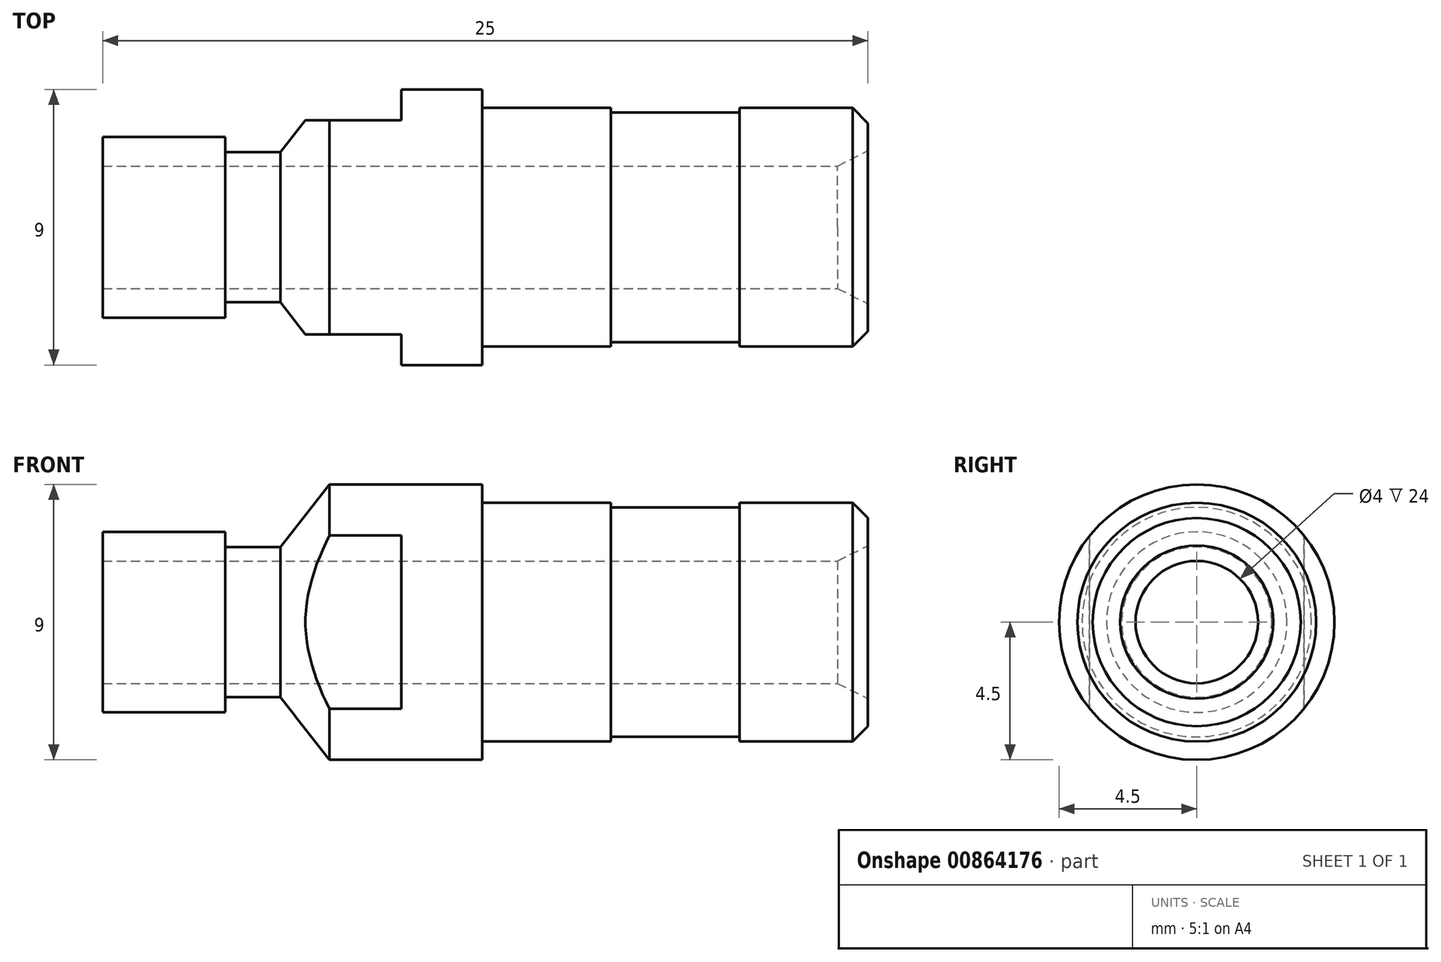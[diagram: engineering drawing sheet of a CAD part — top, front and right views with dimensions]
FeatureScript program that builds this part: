
annotation { "Feature Type Name" : "Feature", "Feature Type Description" : "" }
export const myFeature = defineFeature(function(context is Context, id is Id, definition is map)
    precondition{}
    {
        {
            var Q0;
            Q0=qCreatedBy(makeId("Front.planeOp"),FACE);
            var sketch = newSketch(context, id + "F0", { "sketchPlane" : qUnion([Q0])});
            skLineSegment(sketch, "E0", {"start": v(0, 0) * mm, "end": v(0, 2.95) * mm, "construction": true});
            skLineSegment(sketch, "E1", {"start": v(0, 2.95) * mm, "end": v(4, 2.95) * mm});
            skLineSegment(sketch, "E2", {"start": v(4, 2.95) * mm, "end": v(4, 2.45) * mm});
            skLineSegment(sketch, "E3", {"start": v(4, 2.45) * mm, "end": v(5.8, 2.45) * mm});
            skLineSegment(sketch, "E4", {"start": v(5.8, 2.45) * mm, "end": v(7.4, 4.5) * mm});
            skLineSegment(sketch, "E5", {"start": v(7.4, 4.5) * mm, "end": v(12.4, 4.5) * mm});
            skLineSegment(sketch, "E6", {"start": v(12.4, 4.5) * mm, "end": v(12.4, 3.9) * mm});
            skLineSegment(sketch, "E7", {"start": v(12.4, 3.9) * mm, "end": v(16.6, 3.9) * mm});
            skLineSegment(sketch, "E8", {"start": v(16.6, 3.9) * mm, "end": v(16.6, 3.75) * mm});
            skLineSegment(sketch, "E9", {"start": v(16.6, 3.75) * mm, "end": v(20.8, 3.75) * mm});
            skLineSegment(sketch, "E10", {"start": v(20.8, 3.75) * mm, "end": v(20.8, 3.9) * mm});
            skLineSegment(sketch, "E11", {"start": v(20.8, 3.9) * mm, "end": v(25, 3.9) * mm});
            skLineSegment(sketch, "E12", {"start": v(25, 3.9) * mm, "end": v(25, 2) * mm});
            skLineSegment(sketch, "E13", {"start": v(39.23, 0) * mm, "end": v(0, 0) * mm, "construction": true});
            skLineSegment(sketch, "E14", {"start": v(0, 2.95) * mm, "end": v(0, 2) * mm});
            skLineSegment(sketch, "E15", {"start": v(0, 2) * mm, "end": v(25, 2) * mm});
            skSolve(sketch);
        }
        {
            var Q0;
            Q0 = qSketchRegion(id + "F0", true);
            var Q1;
            Q1=sQuery(id+"F0.wireOp",EDGE,"E13");
            revolve(context, id + "F1", {"surfaceOperationType" : NewSurfaceOperationType.NEW, "entities" : qUnion([Q0]), "axis" : qUnion([Q1]), "revolveType" : RevolveType.FULL});
        }
        {
            var Q0;
            Q0=makeQuery(id+"F1.opRevolve","SWEPT_EDGE",EDGE,{"disambiguationData":[OSD([sQuery(id+"F0.wireOp",EDGE,"E11"),sQuery(id+"F0.wireOp",EDGE,"E12")])]});
            chamfer(context, id + "F2", {"entities" : qUnion([Q0]), "width" : .5 * mm, "tangentPropagation" : true});
        }
        {
            var Q0;
            Q0=makeQuery(id+"F1.opRevolve","SWEPT_EDGE",EDGE,{"disambiguationData":[OSD([sQuery(id+"F0.wireOp",EDGE,"E12"),sQuery(id+"F0.wireOp",EDGE,"E15")])]});
            chamfer(context, id + "F3", {"entities" : qUnion([Q0]), "chamferType" : ChamferType.TWO_OFFSETS, "width1" : 1 * mm, "oppositeDirection" : false, "width2" : .5 * mm, "tangentPropagation" : true});
        }
        {
            var Q0;
            Q0=qCreatedBy(makeId("Top.planeOp"),FACE);
            var sketch = newSketch(context, id + "F4", { "sketchPlane" : qUnion([Q0])});
            skLineSegment(sketch, "E16.bottom", {"start": v(5.75, 3.5) * mm, "end": v(9.75, 3.5) * mm});
            skLineSegment(sketch, "E16.top", {"start": v(5.75, -3.5) * mm, "end": v(9.75, -3.5) * mm});
            skLineSegment(sketch, "E16.left", {"start": v(5.75, 3.5) * mm, "end": v(5.75, -3.5) * mm, "construction": true});
            skLineSegment(sketch, "E16.right", {"start": v(9.75, 3.5) * mm, "end": v(9.75, -3.5) * mm, "construction": true});
            skLineSegment(sketch, "E17", {"start": v(5.75, 0) * mm, "end": v(0, 0) * mm, "construction": true});
            skLineSegment(sketch, "E18", {"start": v(5.75, 3.5) * mm, "end": v(5.75, 5.5) * mm});
            skLineSegment(sketch, "E19", {"start": v(5.75, 5.5) * mm, "end": v(9.75, 5.5) * mm});
            skLineSegment(sketch, "E20", {"start": v(9.75, 5.5) * mm, "end": v(9.75, 3.5) * mm});
            skLineSegment(sketch, "E21", {"start": v(9.75, -3.5) * mm, "end": v(9.75, -5.5) * mm});
            skLineSegment(sketch, "E22", {"start": v(9.75, -5.5) * mm, "end": v(5.75, -5.5) * mm});
            skLineSegment(sketch, "E23", {"start": v(5.75, -5.5) * mm, "end": v(5.75, -3.5) * mm});
            skSolve(sketch);
        }
        {
            var Q0;
            Q0 = qSketchRegion(id + "F4", true);
            extrude(context, id + "F5", {"entities" : qUnion([Q0]), "operationType" : NewBodyOperationType.REMOVE, "endBound" : BoundingType.SYMMETRIC, "oppositeDirection" : true, "depth" : 25 * mm, "offsetDistance" : 25 * mm});
        }
    });
